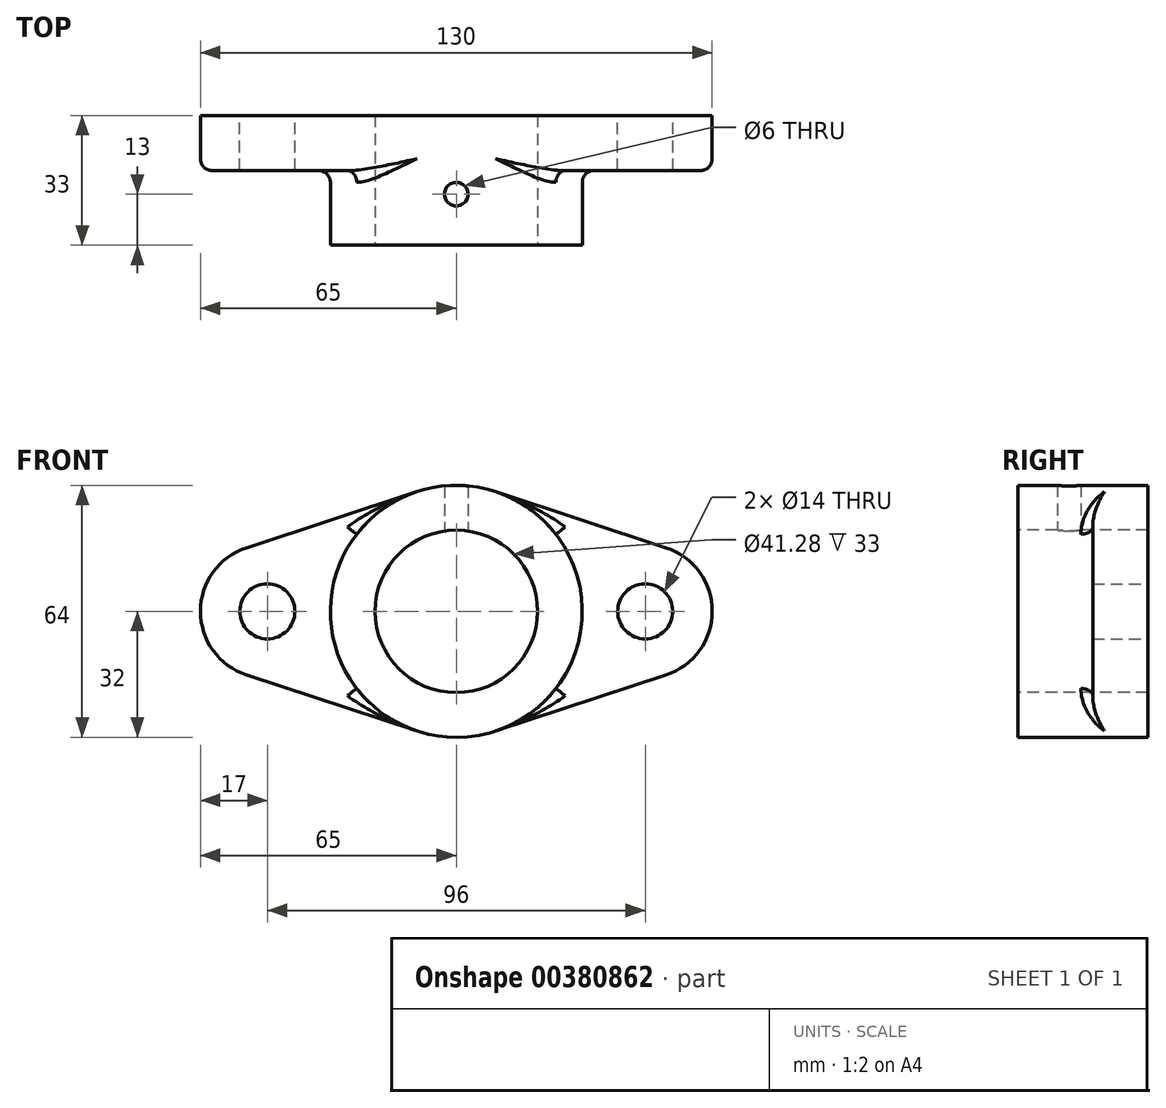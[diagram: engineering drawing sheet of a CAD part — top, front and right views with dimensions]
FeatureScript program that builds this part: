
annotation { "Feature Type Name" : "Feature", "Feature Type Description" : "" }
export const myFeature = defineFeature(function(context is Context, id is Id, definition is map)
    precondition{}
    {
        {
            var Q0;
            Q0=qCreatedBy(makeId("Front.planeOp"),FACE);
            var sketch = newSketch(context, id + "F0", { "sketchPlane" : qUnion([Q0])});
            skCircle(sketch, "E0", {"center": v(0, 0) * mm, "radius": 32 * mm});
            skCircle(sketch, "E1", {"center": v(48, 0) * mm, "radius": 7 * mm});
            skCircle(sketch, "E2", {"center": v(-48, 0) * mm, "radius": 7 * mm});
            skArc(sketch, "E3", {"start": v(-53.31, 16.15) * mm, "mid": v(-65, 0) * mm, "end": v(-53.31, -16.15) * mm});
            skArc(sketch, "E4.MirrorCS", {"start": v(53.31, 16.15) * mm, "mid": v(65, 0) * mm, "end": v(53.31, -16.15) * mm});
            skLineSegment(sketch, "E5", {"start": v(-53.31, 16.15) * mm, "end": v(-10, 30.4) * mm});
            skLineSegment(sketch, "E6", {"start": v(53.31, 16.15) * mm, "end": v(10, 30.4) * mm});
            skLineSegment(sketch, "E7", {"start": v(-53.31, -16.15) * mm, "end": v(-10, -30.4) * mm});
            skLineSegment(sketch, "E8", {"start": v(53.31, -16.15) * mm, "end": v(10, -30.4) * mm});
            skPoint(sketch, "E9.orphan", {"position": v(-35.09, 11.06) * mm});
            skPoint(sketch, "E10.orphan", {"position": v(-35.09, -11.06) * mm});
            skPoint(sketch, "E11.orphan", {"position": v(35.09, -11.06) * mm});
            skPoint(sketch, "E12.orphan", {"position": v(35.09, 11.06) * mm});
            skSolve(sketch);
        }
        {
            var Q0;
            {var subQ0=sQuery(id+"F0.wireOp",EDGE,"E0");var subQ1=makeQuery(id+"F0.imprint","INTERSECT",VERTEX,{"derivedFrom":[subQ0,sQuery(id+"F0.wireOp",EDGE,"uLL8ISus-9Av7-iyRI-kB87-lmHixwpDaEE1")]});Q0=makeQuery(id+"F0.imprint","IMPRINT",FACE,{"disambiguationData":[TD([[makeQuery(id+"F0.imprint","IMPRINT",EDGE,{"disambiguationData":[TD([[subQ1,1.0]])],"derivedFrom":subQ0}),1.0]])]});}
            extrude(context, id + "F1", {"entities" : qUnion([Q0]), "depth" : 33 * mm});
        }
        {
            var Q0;
            Q0 = qSketchRegion(id + "F0", true);
            extrude(context, id + "F2", {"entities" : qUnion([Q0]), "operationType" : NewBodyOperationType.ADD, "depth" : 14 * mm});
        }
        {
            var Q0;
            Q0=makeQuery(id+"F1.opExtrude","CAP_FACE",FACE,{"disambiguationData":[OSD([sQuery(id+"F0.wireOp",EDGE,"E0")])],"isStart":false});
            var sketch = newSketch(context, id + "F3", { "sketchPlane" : qUnion([Q0])});
            skCircle(sketch, "E13", {"center": v(0, 0) * mm, "radius": 20.64 * mm});
            skSolve(sketch);
        }
        {
            var Q0;
            Q0=makeQuery(id+"F3.imprint","IMPRINT",FACE,{"disambiguationData":[TD([[makeQuery(id+"F3.imprint","IMPRINT",EDGE,{"derivedFrom":sQuery(id+"F3.wireOp",EDGE,"E13")}),1.0]])]});
            extrude(context, id + "F4", {"entities" : qUnion([Q0]), "operationType" : NewBodyOperationType.REMOVE, "endBound" : BoundingType.THROUGH_ALL, "oppositeDirection" : true, "depth" : 25 * mm});
        }
        {
            var Q0;
            {var subQ0=sQuery(id+"F0.wireOp",EDGE,"E0");Q0=makeQuery(id+"F2.boolean.opBoolean","INTERSECT",EDGE,{"disambiguationData":[OD(1.0)],"derivedFrom":[makeQuery(id+"F1.opExtrude","SWEPT_FACE",FACE,{"disambiguationData":[OSD([subQ0])]}),makeQuery(id+"F2.opExtrude","CAP_FACE",FACE,{"disambiguationData":[OSD([subQ0,sQuery(id+"F0.wireOp",EDGE,"E1"),sQuery(id+"F0.wireOp",EDGE,"E2"),sQuery(id+"F0.wireOp",EDGE,"E3"),sQuery(id+"F0.wireOp",EDGE,"E4.MirrorCS"),sQuery(id+"F0.wireOp",EDGE,"E5"),sQuery(id+"F0.wireOp",EDGE,"E6"),sQuery(id+"F0.wireOp",EDGE,"E7"),sQuery(id+"F0.wireOp",EDGE,"E8")])],"isStart":false})]});}
            var Q1;
            Q1=makeQuery(id+"F2.opExtrude","CAP_EDGE",EDGE,{"disambiguationData":[OSD([sQuery(id+"F0.wireOp",EDGE,"E8")])],"isStart":false});
            var Q2;
            {var subQ0=sQuery(id+"F0.wireOp",EDGE,"E0");Q2=makeQuery(id+"F2.boolean.opBoolean","INTERSECT",EDGE,{"disambiguationData":[OD(0.0)],"derivedFrom":[makeQuery(id+"F1.opExtrude","SWEPT_FACE",FACE,{"disambiguationData":[OSD([subQ0])]}),makeQuery(id+"F2.opExtrude","CAP_FACE",FACE,{"disambiguationData":[OSD([subQ0,sQuery(id+"F0.wireOp",EDGE,"E1"),sQuery(id+"F0.wireOp",EDGE,"E2"),sQuery(id+"F0.wireOp",EDGE,"E3"),sQuery(id+"F0.wireOp",EDGE,"E4.MirrorCS"),sQuery(id+"F0.wireOp",EDGE,"E5"),sQuery(id+"F0.wireOp",EDGE,"E6"),sQuery(id+"F0.wireOp",EDGE,"E7"),sQuery(id+"F0.wireOp",EDGE,"E8")])],"isStart":false})]});}
            var Q3;
            Q3=makeQuery(id+"F2.opExtrude","CAP_EDGE",EDGE,{"disambiguationData":[OSD([sQuery(id+"F0.wireOp",EDGE,"E7")])],"isStart":false});
            fillet(context, id + "F5", {"entities" : qUnion([Q0, Q1, Q2, Q3]), "radius" : 3 * mm, "tangentPropagation" : true, "allowEdgeOverflow" : false});
        }
        {
            var Q0;
            Q0=qCreatedBy(makeId("Top.planeOp"),FACE);
            var sketch = newSketch(context, id + "F6", { "sketchPlane" : qUnion([Q0])});
            skCircle(sketch, "E14", {"center": v(0, -20) * mm, "radius": 3 * mm});
            skSolve(sketch);
        }
        {
            var Q0;
            Q0=makeQuery(id+"F6.imprint","IMPRINT",FACE,{"disambiguationData":[TD([[makeQuery(id+"F6.imprint","IMPRINT",EDGE,{"derivedFrom":sQuery(id+"F6.wireOp",EDGE,"E14")}),1.0]])]});
            extrude(context, id + "F7", {"entities" : qUnion([Q0]), "operationType" : NewBodyOperationType.REMOVE, "depth" : 88 * mm});
        }
    });
